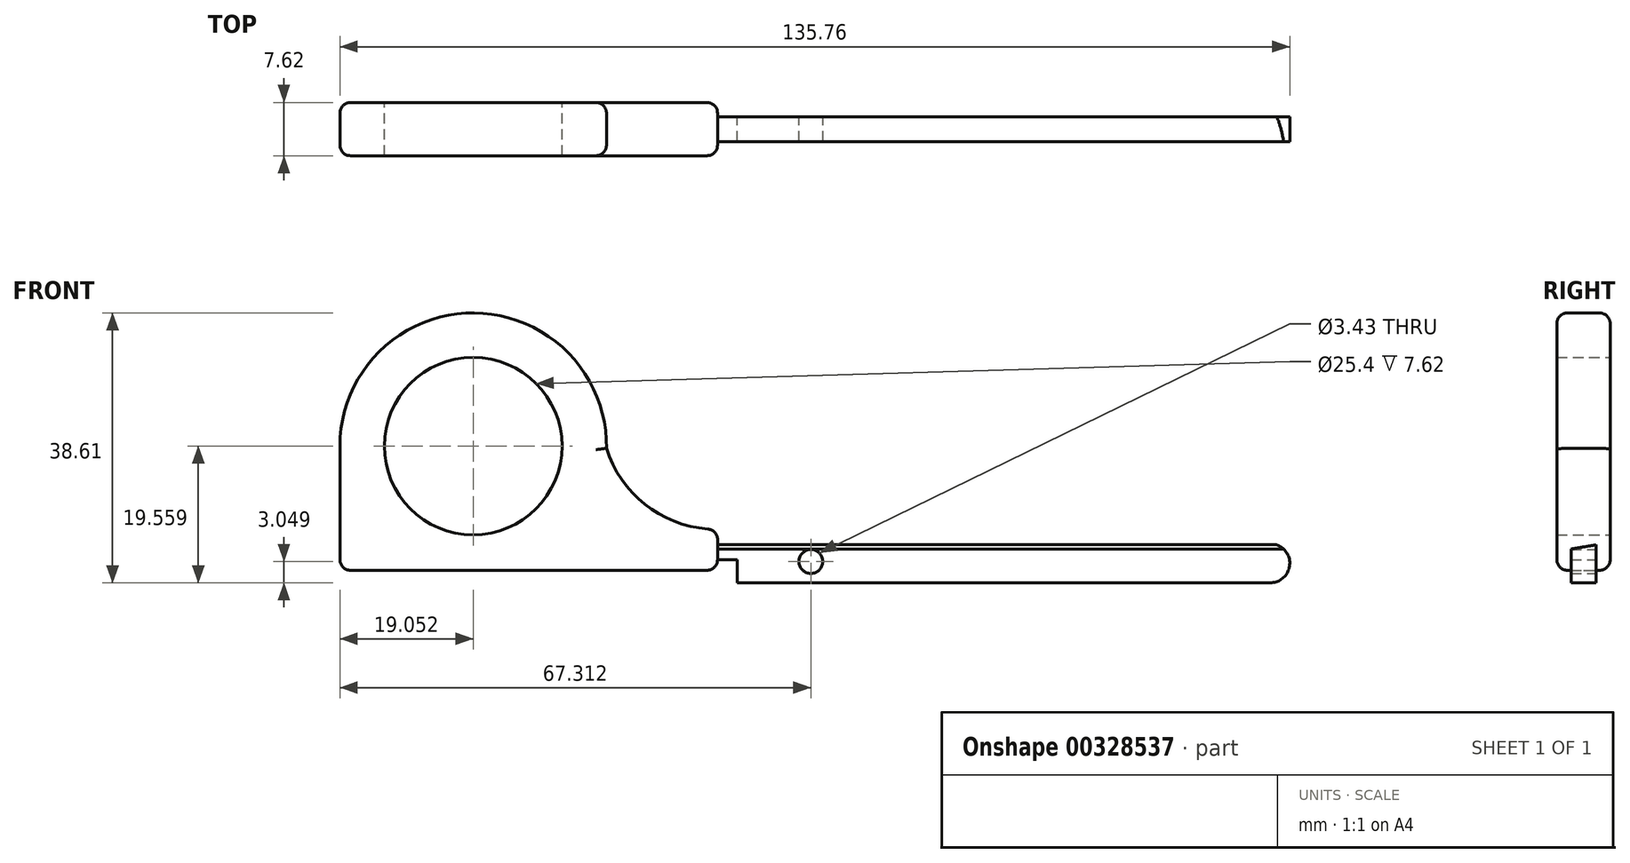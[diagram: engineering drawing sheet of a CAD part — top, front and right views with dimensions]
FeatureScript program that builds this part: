
annotation { "Feature Type Name" : "Feature", "Feature Type Description" : "" }
export const myFeature = defineFeature(function(context is Context, id is Id, definition is map)
    precondition{}
    {
        {
            var Q0;
            Q0=qCreatedBy(makeId("Front.planeOp"),FACE);
            var sketch = newSketch(context, id + "F0", { "sketchPlane" : qUnion([Q0])});
            skLineSegment(sketch, "E0", {"start": v(-33.84, -6.02) * mm, "end": v(17.08, -6.02) * mm});
            skLineSegment(sketch, "E1", {"start": v(18.6, -4.5) * mm, "end": v(18.6, -1.62) * mm});
            skLineSegment(sketch, "E2", {"start": v(-35.37, -4.5) * mm, "end": v(-35.37, 11.76) * mm});
            skArc(sketch, "E3", {"start": v(2.73, 11.45) * mm, "mid": v(8.2, 3.45) * mm, "end": v(17.2, -0.1) * mm});
            skArc(sketch, "E4", {"start": v(2.73, 11.45) * mm, "mid": v(-16.16, 30.8) * mm, "end": v(-35.37, 11.76) * mm});
            skCircle(sketch, "E5", {"center": v(-16.32, 11.76) * mm, "radius": 12.7 * mm});
            skPoint(sketch, "E6.visualSharp", {"position": v(18.6, -0.15) * mm});
            skArc(sketch, "E6.filletArc", {"start": v(18.6, -1.62) * mm, "mid": v(18.2, -0.59) * mm, "end": v(17.2, -0.1) * mm});
            skPoint(sketch, "E7.visualSharp", {"position": v(18.6, -6.02) * mm});
            skArc(sketch, "E7.filletArc", {"start": v(17.08, -6.02) * mm, "mid": v(18.16, -5.57) * mm, "end": v(18.6, -4.5) * mm});
            skPoint(sketch, "E8.visualSharp", {"position": v(-35.37, -6.02) * mm});
            skArc(sketch, "E8.filletArc", {"start": v(-35.37, -4.5) * mm, "mid": v(-34.92, -5.57) * mm, "end": v(-33.84, -6.02) * mm});
            skLineSegment(sketch, "E9", {"start": v(97.6, -7.8) * mm, "end": v(21.4, -7.8) * mm});
            skLineSegment(sketch, "E10", {"start": v(21.4, -7.8) * mm, "end": v(21.4, -4.5) * mm});
            skLineSegment(sketch, "E11", {"start": v(21.4, -4.5) * mm, "end": v(18.6, -4.5) * mm});
            skLineSegment(sketch, "E12", {"start": v(18.6, -2.21) * mm, "end": v(97.6, -2.21) * mm});
            skLineSegment(sketch, "E13", {"start": v(21.4, -4.5) * mm, "end": v(21.4, -4.75) * mm, "construction": true});
            skLineSegment(sketch, "E14", {"start": v(21.4, -4.75) * mm, "end": v(31.94, -4.75) * mm, "construction": true});
            skCircle(sketch, "E15", {"center": v(31.94, -4.75) * mm, "radius": 1.71 * mm});
            skArc(sketch, "E16", {"start": v(97.6, -7.8) * mm, "mid": v(100.4, -5) * mm, "end": v(97.6, -2.21) * mm});
            skSolve(sketch);
        }
        {
            var Q0;
            Q0=makeQuery(id+"F0.imprint","IMPRINT",FACE,{"disambiguationData":[TD([[makeQuery(id+"F0.imprint","IMPRINT",EDGE,{"derivedFrom":sQuery(id+"F0.wireOp",EDGE,"E9")}),-1.0]])]});
            extrude(context, id + "F1", {"entities" : qUnion([Q0]), "endBound" : BoundingType.SYMMETRIC, "depth" : 3.56 * mm});
        }
        {
            var Q0;
            Q0=makeQuery(id+"F0.imprint","IMPRINT",FACE,{"disambiguationData":[TD([[makeQuery(id+"F0.imprint","IMPRINT",EDGE,{"derivedFrom":sQuery(id+"F0.wireOp",EDGE,"E0")}),1.0]])]});
            extrude(context, id + "F2", {"entities" : qUnion([Q0]), "operationType" : NewBodyOperationType.ADD, "endBound" : BoundingType.SYMMETRIC, "depth" : 7.62 * mm});
        }
        {
            var Q0;
            Q0=makeQuery(id+"F2.opExtrude","CAP_EDGE",EDGE,{"disambiguationData":[OSD([sQuery(id+"F0.wireOp",EDGE,"E4")])],"isStart":false});
            var Q1;
            Q1=makeQuery(id+"F2.opExtrude","CAP_EDGE",EDGE,{"disambiguationData":[OSD([sQuery(id+"F0.wireOp",EDGE,"E4")])],"isStart":true});
            fillet(context, id + "F3", {"entities" : qUnion([Q0, Q1]), "radius" : 1.52 * mm, "tangentPropagation" : true, "allowEdgeOverflow" : false});
        }
        {
            var Q0;
            Q0=makeQuery(id+"F2.opExtrude","SWEPT_FACE",FACE,{"disambiguationData":[OSD([sQuery(id+"F0.wireOp",EDGE,"E1")])]});
            var sketch = newSketch(context, id + "F4", { "sketchPlane" : qUnion([Q0])});
            skPoint(sketch, "E17.endSnap0", {"position": v(0, -1.62) * mm});
            skLineSegment(sketch, "E18", {"start": v(-2.29, -3.06) * mm, "end": v(2.7, -2.21) * mm});
            skLineSegment(sketch, "E19", {"start": v(2.7, -2.21) * mm, "end": v(-2.29, -2.21) * mm});
            skLineSegment(sketch, "E20", {"start": v(-2.29, -2.21) * mm, "end": v(-2.29, -3.06) * mm});
            skSolve(sketch);
        }
        {
            var Q0;
            Q0 = qSketchRegion(id + "F4", true);
            extrude(context, id + "F5", {"entities" : qUnion([Q0]), "operationType" : NewBodyOperationType.REMOVE, "endBound" : BoundingType.THROUGH_ALL, "depth" : 25.4 * mm});
        }
        {
            var Q0;
            Q0 = qSketchRegion(id + "F4", true);
            extrude(context, id + "F6", {"entities" : qUnion([Q0]), "operationType" : NewBodyOperationType.REMOVE, "endBound" : BoundingType.THROUGH_ALL, "depth" : 25.4 * mm});
        }
    });
